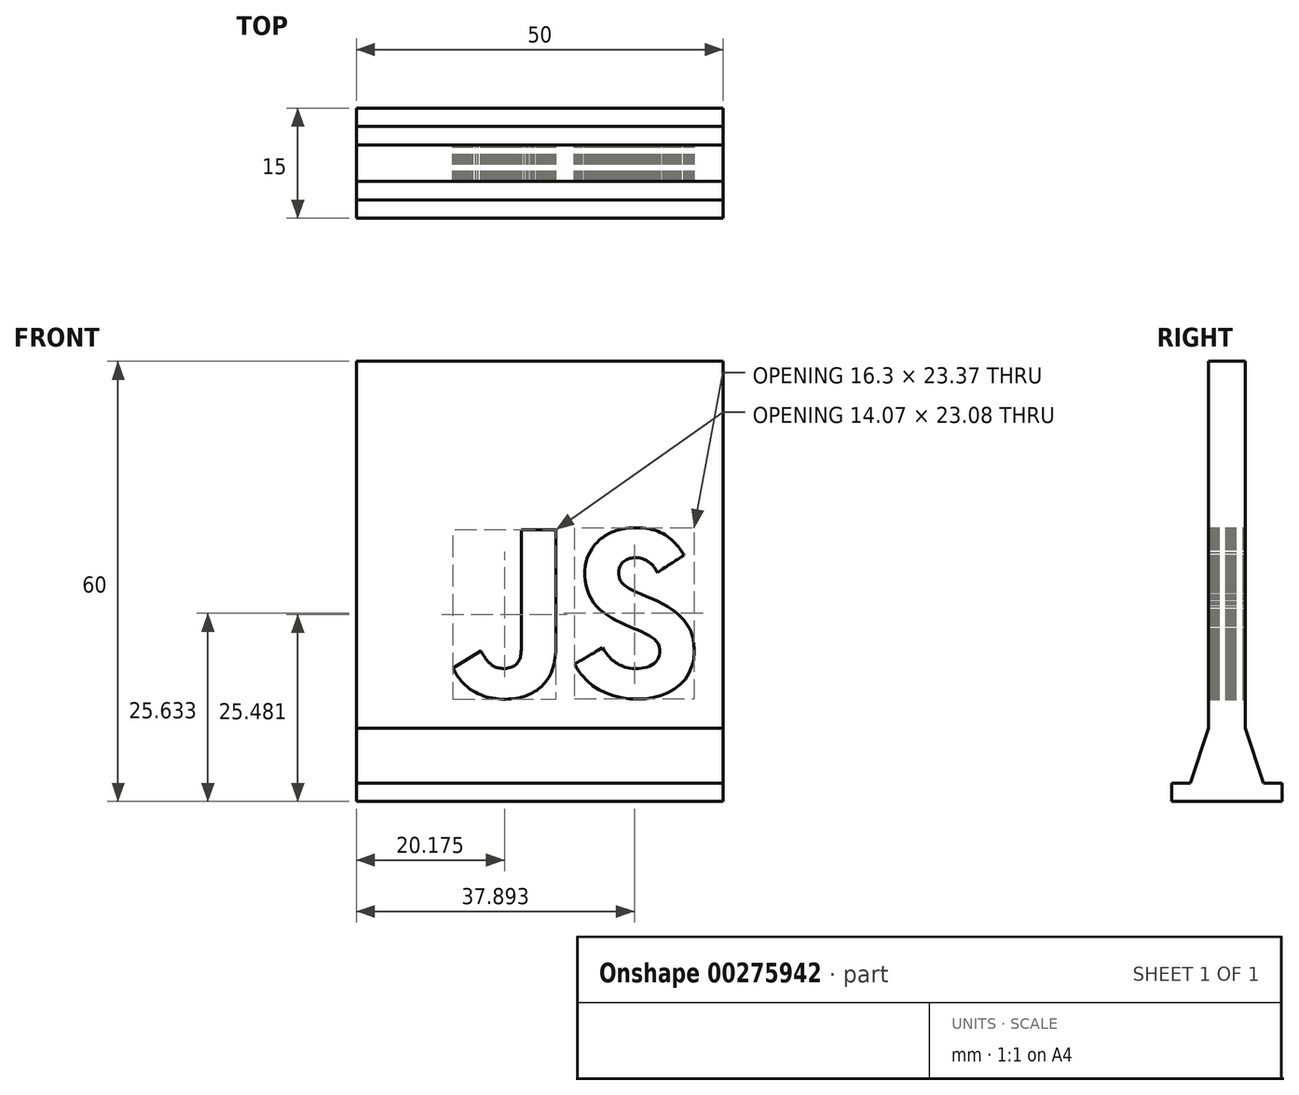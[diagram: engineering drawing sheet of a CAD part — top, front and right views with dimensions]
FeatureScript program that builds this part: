
annotation { "Feature Type Name" : "Feature", "Feature Type Description" : "" }
export const myFeature = defineFeature(function(context is Context, id is Id, definition is map)
    precondition{}
    {
        {
            var Q0;
            Q0=qCreatedBy(makeId("Front.planeOp"),FACE);
            var sketch = newSketch(context, id + "F0", { "sketchPlane" : qUnion([Q0])});
            skLineSegment(sketch, "E0", {"start": v(-25, 25) * mm, "end": v(-21.87, 25) * mm});
            skLineSegment(sketch, "E1", {"start": v(-21.87, 25) * mm, "end": v(-18.75, 25) * mm});
            skLineSegment(sketch, "E2", {"start": v(-18.75, 25) * mm, "end": v(-15.62, 25) * mm});
            skLineSegment(sketch, "E3", {"start": v(-15.62, 25) * mm, "end": v(-12.5, 25) * mm});
            skLineSegment(sketch, "E4", {"start": v(-12.5, 25) * mm, "end": v(-9.37, 25) * mm});
            skLineSegment(sketch, "E5", {"start": v(-9.37, 25) * mm, "end": v(-6.25, 25) * mm});
            skLineSegment(sketch, "E6", {"start": v(-6.25, 25) * mm, "end": v(-3.12, 25) * mm});
            skLineSegment(sketch, "E7", {"start": v(-3.12, 25) * mm, "end": v(0, 25) * mm});
            skLineSegment(sketch, "E8", {"start": v(0, 25) * mm, "end": v(3.12, 25) * mm});
            skLineSegment(sketch, "E9", {"start": v(3.12, 25) * mm, "end": v(6.25, 25) * mm});
            skLineSegment(sketch, "E10", {"start": v(6.25, 25) * mm, "end": v(9.37, 25) * mm});
            skLineSegment(sketch, "E11", {"start": v(9.37, 25) * mm, "end": v(12.5, 25) * mm});
            skLineSegment(sketch, "E12", {"start": v(12.5, 25) * mm, "end": v(15.62, 25) * mm});
            skLineSegment(sketch, "E13", {"start": v(15.62, 25) * mm, "end": v(18.75, 25) * mm});
            skLineSegment(sketch, "E14", {"start": v(18.75, 25) * mm, "end": v(21.87, 25) * mm});
            skLineSegment(sketch, "E15", {"start": v(21.87, 25) * mm, "end": v(25, 25) * mm});
            skLineSegment(sketch, "E16", {"start": v(25, 25) * mm, "end": v(25, 21.87) * mm});
            skLineSegment(sketch, "E17", {"start": v(25, 21.87) * mm, "end": v(25, 18.75) * mm});
            skLineSegment(sketch, "E18", {"start": v(25, 18.75) * mm, "end": v(25, 15.62) * mm});
            skLineSegment(sketch, "E19", {"start": v(25, 15.62) * mm, "end": v(25, 12.5) * mm});
            skLineSegment(sketch, "E20", {"start": v(25, 12.5) * mm, "end": v(25, 9.37) * mm});
            skLineSegment(sketch, "E21", {"start": v(25, 9.37) * mm, "end": v(25, 6.25) * mm});
            skLineSegment(sketch, "E22", {"start": v(25, 6.25) * mm, "end": v(25, 3.12) * mm});
            skLineSegment(sketch, "E23", {"start": v(25, 3.12) * mm, "end": v(25, 0) * mm});
            skLineSegment(sketch, "E24", {"start": v(25, 0) * mm, "end": v(25, -3.13) * mm});
            skLineSegment(sketch, "E25", {"start": v(25, -3.13) * mm, "end": v(25, -6.25) * mm});
            skLineSegment(sketch, "E26", {"start": v(25, -6.25) * mm, "end": v(25, -9.38) * mm});
            skLineSegment(sketch, "E27", {"start": v(25, -9.38) * mm, "end": v(25, -12.5) * mm});
            skLineSegment(sketch, "E28", {"start": v(25, -12.5) * mm, "end": v(25, -15.63) * mm});
            skLineSegment(sketch, "E29", {"start": v(25, -15.63) * mm, "end": v(25, -18.75) * mm});
            skLineSegment(sketch, "E30", {"start": v(25, -18.75) * mm, "end": v(25, -21.88) * mm});
            skLineSegment(sketch, "E31", {"start": v(25, -21.88) * mm, "end": v(25, -25) * mm});
            skLineSegment(sketch, "E32", {"start": v(25, -25) * mm, "end": v(21.87, -25) * mm});
            skLineSegment(sketch, "E33", {"start": v(21.87, -25) * mm, "end": v(18.75, -25) * mm});
            skLineSegment(sketch, "E34", {"start": v(18.75, -25) * mm, "end": v(15.62, -25) * mm});
            skLineSegment(sketch, "E35", {"start": v(15.62, -25) * mm, "end": v(12.5, -25) * mm});
            skLineSegment(sketch, "E36", {"start": v(12.5, -25) * mm, "end": v(9.37, -25) * mm});
            skLineSegment(sketch, "E37", {"start": v(9.37, -25) * mm, "end": v(6.25, -25) * mm});
            skLineSegment(sketch, "E38", {"start": v(6.25, -25) * mm, "end": v(3.12, -25) * mm});
            skLineSegment(sketch, "E39", {"start": v(3.12, -25) * mm, "end": v(0, -25) * mm});
            skLineSegment(sketch, "E40", {"start": v(0, -25) * mm, "end": v(-3.12, -25) * mm});
            skLineSegment(sketch, "E41", {"start": v(-3.12, -25) * mm, "end": v(-6.25, -25) * mm});
            skLineSegment(sketch, "E42", {"start": v(-6.25, -25) * mm, "end": v(-9.37, -25) * mm});
            skLineSegment(sketch, "E43", {"start": v(-9.37, -25) * mm, "end": v(-12.5, -25) * mm});
            skLineSegment(sketch, "E44", {"start": v(-12.5, -25) * mm, "end": v(-15.62, -25) * mm});
            skLineSegment(sketch, "E45", {"start": v(-15.62, -25) * mm, "end": v(-18.75, -25) * mm});
            skLineSegment(sketch, "E46", {"start": v(-18.75, -25) * mm, "end": v(-21.87, -25) * mm});
            skLineSegment(sketch, "E47", {"start": v(-21.87, -25) * mm, "end": v(-25, -25) * mm});
            skLineSegment(sketch, "E48", {"start": v(-25, -25) * mm, "end": v(-25, -21.88) * mm});
            skLineSegment(sketch, "E49", {"start": v(-25, -21.88) * mm, "end": v(-25, -18.75) * mm});
            skLineSegment(sketch, "E50", {"start": v(-25, -18.75) * mm, "end": v(-25, -15.63) * mm});
            skLineSegment(sketch, "E51", {"start": v(-25, -15.63) * mm, "end": v(-25, -12.5) * mm});
            skLineSegment(sketch, "E52", {"start": v(-25, -12.5) * mm, "end": v(-25, -9.38) * mm});
            skLineSegment(sketch, "E53", {"start": v(-25, -9.38) * mm, "end": v(-25, -6.25) * mm});
            skLineSegment(sketch, "E54", {"start": v(-25, -6.25) * mm, "end": v(-25, -3.13) * mm});
            skLineSegment(sketch, "E55", {"start": v(-25, -3.13) * mm, "end": v(-25, 0) * mm});
            skLineSegment(sketch, "E56", {"start": v(-25, 0) * mm, "end": v(-25, 3.12) * mm});
            skLineSegment(sketch, "E57", {"start": v(-25, 3.12) * mm, "end": v(-25, 6.25) * mm});
            skLineSegment(sketch, "E58", {"start": v(-25, 6.25) * mm, "end": v(-25, 9.37) * mm});
            skLineSegment(sketch, "E59", {"start": v(-25, 9.37) * mm, "end": v(-25, 12.5) * mm});
            skLineSegment(sketch, "E60", {"start": v(-25, 12.5) * mm, "end": v(-25, 15.62) * mm});
            skLineSegment(sketch, "E61", {"start": v(-25, 15.62) * mm, "end": v(-25, 18.75) * mm});
            skLineSegment(sketch, "E62", {"start": v(-25, 18.75) * mm, "end": v(-25, 21.87) * mm});
            skLineSegment(sketch, "E63", {"start": v(-25, 21.87) * mm, "end": v(-25, 25) * mm});
            skLineSegment(sketch, "E64", {"start": v(20.9, -13.07) * mm, "end": v(20.83, -12.65) * mm});
            skLineSegment(sketch, "E65", {"start": v(20.83, -12.65) * mm, "end": v(20.71, -12.24) * mm});
            skLineSegment(sketch, "E66", {"start": v(20.71, -12.24) * mm, "end": v(20.57, -11.83) * mm});
            skLineSegment(sketch, "E67", {"start": v(20.57, -11.83) * mm, "end": v(20.4, -11.43) * mm});
            skLineSegment(sketch, "E68", {"start": v(20.4, -11.43) * mm, "end": v(20.18, -11.04) * mm});
            skLineSegment(sketch, "E69", {"start": v(20.18, -11.04) * mm, "end": v(19.93, -10.65) * mm});
            skLineSegment(sketch, "E70", {"start": v(19.93, -10.65) * mm, "end": v(19.63, -10.27) * mm});
            skLineSegment(sketch, "E71", {"start": v(19.63, -10.27) * mm, "end": v(19.3, -9.9) * mm});
            skLineSegment(sketch, "E72", {"start": v(19.3, -9.9) * mm, "end": v(18.9, -9.53) * mm});
            skLineSegment(sketch, "E73", {"start": v(18.9, -9.53) * mm, "end": v(18.47, -9.17) * mm});
            skLineSegment(sketch, "E74", {"start": v(18.47, -9.17) * mm, "end": v(17.98, -8.81) * mm});
            skLineSegment(sketch, "E75", {"start": v(17.98, -8.81) * mm, "end": v(17.43, -8.46) * mm});
            skLineSegment(sketch, "E76", {"start": v(17.43, -8.46) * mm, "end": v(16.83, -8.11) * mm});
            skLineSegment(sketch, "E77", {"start": v(16.83, -8.11) * mm, "end": v(16.17, -7.77) * mm});
            skLineSegment(sketch, "E78", {"start": v(16.17, -7.77) * mm, "end": v(15.44, -7.43) * mm});
            skLineSegment(sketch, "E79", {"start": v(15.44, -7.43) * mm, "end": v(14.65, -7.1) * mm});
            skLineSegment(sketch, "E80", {"start": v(14.65, -7.1) * mm, "end": v(14.36, -6.96) * mm});
            skLineSegment(sketch, "E81", {"start": v(14.36, -6.96) * mm, "end": v(14.07, -6.84) * mm});
            skLineSegment(sketch, "E82", {"start": v(14.07, -6.84) * mm, "end": v(13.78, -6.71) * mm});
            skLineSegment(sketch, "E83", {"start": v(13.78, -6.71) * mm, "end": v(13.49, -6.59) * mm});
            skLineSegment(sketch, "E84", {"start": v(13.49, -6.59) * mm, "end": v(13.2, -6.46) * mm});
            skLineSegment(sketch, "E85", {"start": v(13.2, -6.46) * mm, "end": v(12.92, -6.34) * mm});
            skLineSegment(sketch, "E86", {"start": v(12.92, -6.34) * mm, "end": v(12.65, -6.21) * mm});
            skLineSegment(sketch, "E87", {"start": v(12.65, -6.21) * mm, "end": v(12.4, -6.08) * mm});
            skLineSegment(sketch, "E88", {"start": v(12.4, -6.08) * mm, "end": v(12.14, -5.94) * mm});
            skLineSegment(sketch, "E89", {"start": v(12.14, -5.94) * mm, "end": v(11.9, -5.8) * mm});
            skLineSegment(sketch, "E90", {"start": v(11.9, -5.8) * mm, "end": v(11.69, -5.65) * mm});
            skLineSegment(sketch, "E91", {"start": v(11.69, -5.65) * mm, "end": v(11.49, -5.48) * mm});
            skLineSegment(sketch, "E92", {"start": v(11.49, -5.48) * mm, "end": v(11.3, -5.31) * mm});
            skLineSegment(sketch, "E93", {"start": v(11.3, -5.31) * mm, "end": v(11.15, -5.13) * mm});
            skLineSegment(sketch, "E94", {"start": v(11.15, -5.13) * mm, "end": v(11.01, -4.93) * mm});
            skLineSegment(sketch, "E95", {"start": v(11.01, -4.93) * mm, "end": v(10.9, -4.72) * mm});
            skLineSegment(sketch, "E96", {"start": v(10.9, -4.72) * mm, "end": v(10.87, -4.6) * mm});
            skLineSegment(sketch, "E97", {"start": v(10.87, -4.6) * mm, "end": v(10.84, -4.48) * mm});
            skLineSegment(sketch, "E98", {"start": v(10.84, -4.48) * mm, "end": v(10.82, -4.37) * mm});
            skLineSegment(sketch, "E99", {"start": v(10.82, -4.37) * mm, "end": v(10.8, -4.27) * mm});
            skLineSegment(sketch, "E100", {"start": v(10.8, -4.27) * mm, "end": v(10.78, -4.17) * mm});
            skLineSegment(sketch, "E101", {"start": v(10.78, -4.17) * mm, "end": v(10.77, -4.07) * mm});
            skLineSegment(sketch, "E102", {"start": v(10.77, -4.07) * mm, "end": v(10.75, -3.98) * mm});
            skLineSegment(sketch, "E103", {"start": v(10.75, -3.98) * mm, "end": v(10.75, -3.9) * mm});
            skLineSegment(sketch, "E104", {"start": v(10.75, -3.9) * mm, "end": v(10.74, -3.8) * mm});
            skLineSegment(sketch, "E105", {"start": v(10.74, -3.8) * mm, "end": v(10.74, -3.73) * mm});
            skLineSegment(sketch, "E106", {"start": v(10.74, -3.73) * mm, "end": v(10.75, -3.65) * mm});
            skLineSegment(sketch, "E107", {"start": v(10.75, -3.65) * mm, "end": v(10.75, -3.57) * mm});
            skLineSegment(sketch, "E108", {"start": v(10.75, -3.57) * mm, "end": v(10.76, -3.49) * mm});
            skLineSegment(sketch, "E109", {"start": v(10.76, -3.49) * mm, "end": v(10.78, -3.41) * mm});
            skLineSegment(sketch, "E110", {"start": v(10.78, -3.41) * mm, "end": v(10.8, -3.34) * mm});
            skLineSegment(sketch, "E111", {"start": v(10.8, -3.34) * mm, "end": v(10.81, -3.26) * mm});
            skLineSegment(sketch, "E112", {"start": v(10.81, -3.26) * mm, "end": v(10.89, -3.02) * mm});
            skLineSegment(sketch, "E113", {"start": v(10.89, -3.02) * mm, "end": v(11, -2.8) * mm});
            skLineSegment(sketch, "E114", {"start": v(11, -2.8) * mm, "end": v(11.12, -2.61) * mm});
            skLineSegment(sketch, "E115", {"start": v(11.12, -2.61) * mm, "end": v(11.27, -2.44) * mm});
            skLineSegment(sketch, "E116", {"start": v(11.27, -2.44) * mm, "end": v(11.44, -2.28) * mm});
            skLineSegment(sketch, "E117", {"start": v(11.44, -2.28) * mm, "end": v(11.63, -2.15) * mm});
            skLineSegment(sketch, "E118", {"start": v(11.63, -2.15) * mm, "end": v(11.83, -2.03) * mm});
            skLineSegment(sketch, "E119", {"start": v(11.83, -2.03) * mm, "end": v(12.05, -1.94) * mm});
            skLineSegment(sketch, "E120", {"start": v(12.05, -1.94) * mm, "end": v(12.28, -1.87) * mm});
            skLineSegment(sketch, "E121", {"start": v(12.28, -1.87) * mm, "end": v(12.51, -1.81) * mm});
            skLineSegment(sketch, "E122", {"start": v(12.51, -1.81) * mm, "end": v(12.75, -1.78) * mm});
            skLineSegment(sketch, "E123", {"start": v(12.75, -1.78) * mm, "end": v(13, -1.77) * mm});
            skLineSegment(sketch, "E124", {"start": v(13, -1.77) * mm, "end": v(13.25, -1.77) * mm});
            skLineSegment(sketch, "E125", {"start": v(13.25, -1.77) * mm, "end": v(13.5, -1.8) * mm});
            skLineSegment(sketch, "E126", {"start": v(13.5, -1.8) * mm, "end": v(13.74, -1.84) * mm});
            skLineSegment(sketch, "E127", {"start": v(13.74, -1.84) * mm, "end": v(13.98, -1.9) * mm});
            skLineSegment(sketch, "E128", {"start": v(13.98, -1.9) * mm, "end": v(14.13, -1.96) * mm});
            skLineSegment(sketch, "E129", {"start": v(14.13, -1.96) * mm, "end": v(14.28, -2.02) * mm});
            skLineSegment(sketch, "E130", {"start": v(14.28, -2.02) * mm, "end": v(14.43, -2.1) * mm});
            skLineSegment(sketch, "E131", {"start": v(14.43, -2.1) * mm, "end": v(14.57, -2.17) * mm});
            skLineSegment(sketch, "E132", {"start": v(14.57, -2.17) * mm, "end": v(14.72, -2.26) * mm});
            skLineSegment(sketch, "E133", {"start": v(14.72, -2.26) * mm, "end": v(14.86, -2.36) * mm});
            skLineSegment(sketch, "E134", {"start": v(14.86, -2.36) * mm, "end": v(15, -2.46) * mm});
            skLineSegment(sketch, "E135", {"start": v(15, -2.46) * mm, "end": v(15.13, -2.57) * mm});
            skLineSegment(sketch, "E136", {"start": v(15.13, -2.57) * mm, "end": v(15.25, -2.7) * mm});
            skLineSegment(sketch, "E137", {"start": v(15.25, -2.7) * mm, "end": v(15.38, -2.83) * mm});
            skLineSegment(sketch, "E138", {"start": v(15.38, -2.83) * mm, "end": v(15.5, -2.96) * mm});
            skLineSegment(sketch, "E139", {"start": v(15.5, -2.96) * mm, "end": v(15.61, -3.11) * mm});
            skLineSegment(sketch, "E140", {"start": v(15.61, -3.11) * mm, "end": v(15.72, -3.27) * mm});
            skLineSegment(sketch, "E141", {"start": v(15.72, -3.27) * mm, "end": v(15.83, -3.43) * mm});
            skLineSegment(sketch, "E142", {"start": v(15.83, -3.43) * mm, "end": v(15.92, -3.6) * mm});
            skLineSegment(sketch, "E143", {"start": v(15.92, -3.6) * mm, "end": v(16.01, -3.79) * mm});
            skLineSegment(sketch, "E144", {"start": v(16.01, -3.79) * mm, "end": v(16.4, -3.54) * mm});
            skLineSegment(sketch, "E145", {"start": v(16.4, -3.54) * mm, "end": v(16.73, -3.33) * mm});
            skLineSegment(sketch, "E146", {"start": v(16.73, -3.33) * mm, "end": v(17.02, -3.13) * mm});
            skLineSegment(sketch, "E147", {"start": v(17.02, -3.13) * mm, "end": v(17.28, -2.97) * mm});
            skLineSegment(sketch, "E148", {"start": v(17.28, -2.97) * mm, "end": v(17.51, -2.82) * mm});
            skLineSegment(sketch, "E149", {"start": v(17.51, -2.82) * mm, "end": v(17.72, -2.68) * mm});
            skLineSegment(sketch, "E150", {"start": v(17.72, -2.68) * mm, "end": v(17.91, -2.56) * mm});
            skLineSegment(sketch, "E151", {"start": v(17.91, -2.56) * mm, "end": v(18.09, -2.45) * mm});
            skLineSegment(sketch, "E152", {"start": v(18.09, -2.45) * mm, "end": v(18.25, -2.34) * mm});
            skLineSegment(sketch, "E153", {"start": v(18.25, -2.34) * mm, "end": v(18.42, -2.24) * mm});
            skLineSegment(sketch, "E154", {"start": v(18.42, -2.24) * mm, "end": v(18.6, -2.13) * mm});
            skLineSegment(sketch, "E155", {"start": v(18.6, -2.13) * mm, "end": v(18.77, -2.02) * mm});
            skLineSegment(sketch, "E156", {"start": v(18.77, -2.02) * mm, "end": v(18.96, -1.9) * mm});
            skLineSegment(sketch, "E157", {"start": v(18.96, -1.9) * mm, "end": v(19.17, -1.76) * mm});
            skLineSegment(sketch, "E158", {"start": v(19.17, -1.76) * mm, "end": v(19.4, -1.6) * mm});
            skLineSegment(sketch, "E159", {"start": v(19.4, -1.6) * mm, "end": v(19.67, -1.44) * mm});
            skLineSegment(sketch, "E160", {"start": v(19.67, -1.44) * mm, "end": v(19.57, -1.29) * mm});
            skLineSegment(sketch, "E161", {"start": v(19.57, -1.29) * mm, "end": v(19.48, -1.14) * mm});
            skLineSegment(sketch, "E162", {"start": v(19.48, -1.14) * mm, "end": v(19.39, -1) * mm});
            skLineSegment(sketch, "E163", {"start": v(19.39, -1) * mm, "end": v(19.3, -0.88) * mm});
            skLineSegment(sketch, "E164", {"start": v(19.3, -0.88) * mm, "end": v(19.22, -0.76) * mm});
            skLineSegment(sketch, "E165", {"start": v(19.22, -0.76) * mm, "end": v(19.14, -0.65) * mm});
            skLineSegment(sketch, "E166", {"start": v(19.14, -0.65) * mm, "end": v(19.07, -0.55) * mm});
            skLineSegment(sketch, "E167", {"start": v(19.07, -0.55) * mm, "end": v(19, -0.45) * mm});
            skLineSegment(sketch, "E168", {"start": v(19, -0.45) * mm, "end": v(18.93, -0.36) * mm});
            skLineSegment(sketch, "E169", {"start": v(18.93, -0.36) * mm, "end": v(18.86, -0.27) * mm});
            skLineSegment(sketch, "E170", {"start": v(18.86, -0.27) * mm, "end": v(18.8, -0.19) * mm});
            skLineSegment(sketch, "E171", {"start": v(18.8, -0.19) * mm, "end": v(18.73, -0.11) * mm});
            skLineSegment(sketch, "E172", {"start": v(18.73, -0.11) * mm, "end": v(18.66, -0.04) * mm});
            skLineSegment(sketch, "E173", {"start": v(18.66, -0.04) * mm, "end": v(18.6, 0.04) * mm});
            skLineSegment(sketch, "E174", {"start": v(18.6, 0.04) * mm, "end": v(18.53, 0.1) * mm});
            skLineSegment(sketch, "E175", {"start": v(18.53, 0.1) * mm, "end": v(18.47, 0.18) * mm});
            skLineSegment(sketch, "E176", {"start": v(18.47, 0.18) * mm, "end": v(18.22, 0.44) * mm});
            skLineSegment(sketch, "E177", {"start": v(18.22, 0.44) * mm, "end": v(17.96, 0.69) * mm});
            skLineSegment(sketch, "E178", {"start": v(17.96, 0.69) * mm, "end": v(17.68, 0.92) * mm});
            skLineSegment(sketch, "E179", {"start": v(17.68, 0.92) * mm, "end": v(17.4, 1.13) * mm});
            skLineSegment(sketch, "E180", {"start": v(17.4, 1.13) * mm, "end": v(17.1, 1.33) * mm});
            skLineSegment(sketch, "E181", {"start": v(17.1, 1.33) * mm, "end": v(16.78, 1.5) * mm});
            skLineSegment(sketch, "E182", {"start": v(16.78, 1.5) * mm, "end": v(16.44, 1.67) * mm});
            skLineSegment(sketch, "E183", {"start": v(16.44, 1.67) * mm, "end": v(16.1, 1.8) * mm});
            skLineSegment(sketch, "E184", {"start": v(16.1, 1.8) * mm, "end": v(15.72, 1.94) * mm});
            skLineSegment(sketch, "E185", {"start": v(15.72, 1.94) * mm, "end": v(15.34, 2.04) * mm});
            skLineSegment(sketch, "E186", {"start": v(15.34, 2.04) * mm, "end": v(14.93, 2.14) * mm});
            skLineSegment(sketch, "E187", {"start": v(14.93, 2.14) * mm, "end": v(14.5, 2.2) * mm});
            skLineSegment(sketch, "E188", {"start": v(14.5, 2.2) * mm, "end": v(14.05, 2.26) * mm});
            skLineSegment(sketch, "E189", {"start": v(14.05, 2.26) * mm, "end": v(13.58, 2.3) * mm});
            skLineSegment(sketch, "E190", {"start": v(13.58, 2.3) * mm, "end": v(13.09, 2.32) * mm});
            skLineSegment(sketch, "E191", {"start": v(13.09, 2.32) * mm, "end": v(12.57, 2.31) * mm});
            skLineSegment(sketch, "E192", {"start": v(12.57, 2.31) * mm, "end": v(12.48, 2.3) * mm});
            skLineSegment(sketch, "E193", {"start": v(12.48, 2.3) * mm, "end": v(12.39, 2.3) * mm});
            skLineSegment(sketch, "E194", {"start": v(12.39, 2.3) * mm, "end": v(12.3, 2.28) * mm});
            skLineSegment(sketch, "E195", {"start": v(12.3, 2.28) * mm, "end": v(12.2, 2.27) * mm});
            skLineSegment(sketch, "E196", {"start": v(12.2, 2.27) * mm, "end": v(12.11, 2.25) * mm});
            skLineSegment(sketch, "E197", {"start": v(12.11, 2.25) * mm, "end": v(12.02, 2.24) * mm});
            skLineSegment(sketch, "E198", {"start": v(12.02, 2.24) * mm, "end": v(11.93, 2.23) * mm});
            skLineSegment(sketch, "E199", {"start": v(11.93, 2.23) * mm, "end": v(11.83, 2.22) * mm});
            skLineSegment(sketch, "E200", {"start": v(11.83, 2.22) * mm, "end": v(11.74, 2.2) * mm});
            skLineSegment(sketch, "E201", {"start": v(11.74, 2.2) * mm, "end": v(11.65, 2.2) * mm});
            skLineSegment(sketch, "E202", {"start": v(11.65, 2.2) * mm, "end": v(11.56, 2.18) * mm});
            skLineSegment(sketch, "E203", {"start": v(11.56, 2.18) * mm, "end": v(11.47, 2.17) * mm});
            skLineSegment(sketch, "E204", {"start": v(11.47, 2.17) * mm, "end": v(11.37, 2.16) * mm});
            skLineSegment(sketch, "E205", {"start": v(11.37, 2.16) * mm, "end": v(11.28, 2.15) * mm});
            skLineSegment(sketch, "E206", {"start": v(11.28, 2.15) * mm, "end": v(11.2, 2.14) * mm});
            skLineSegment(sketch, "E207", {"start": v(11.2, 2.14) * mm, "end": v(11.1, 2.12) * mm});
            skLineSegment(sketch, "E208", {"start": v(11.1, 2.12) * mm, "end": v(10.83, 2.05) * mm});
            skLineSegment(sketch, "E209", {"start": v(10.83, 2.05) * mm, "end": v(10.57, 1.97) * mm});
            skLineSegment(sketch, "E210", {"start": v(10.57, 1.97) * mm, "end": v(10.31, 1.88) * mm});
            skLineSegment(sketch, "E211", {"start": v(10.31, 1.88) * mm, "end": v(10.06, 1.79) * mm});
            skLineSegment(sketch, "E212", {"start": v(10.06, 1.79) * mm, "end": v(9.8, 1.68) * mm});
            skLineSegment(sketch, "E213", {"start": v(9.8, 1.68) * mm, "end": v(9.56, 1.57) * mm});
            skLineSegment(sketch, "E214", {"start": v(9.56, 1.57) * mm, "end": v(9.32, 1.45) * mm});
            skLineSegment(sketch, "E215", {"start": v(9.32, 1.45) * mm, "end": v(9.1, 1.32) * mm});
            skLineSegment(sketch, "E216", {"start": v(9.1, 1.32) * mm, "end": v(8.87, 1.18) * mm});
            skLineSegment(sketch, "E217", {"start": v(8.87, 1.18) * mm, "end": v(8.65, 1.04) * mm});
            skLineSegment(sketch, "E218", {"start": v(8.65, 1.04) * mm, "end": v(8.44, 0.89) * mm});
            skLineSegment(sketch, "E219", {"start": v(8.44, 0.89) * mm, "end": v(8.24, 0.73) * mm});
            skLineSegment(sketch, "E220", {"start": v(8.24, 0.73) * mm, "end": v(8.05, 0.56) * mm});
            skLineSegment(sketch, "E221", {"start": v(8.05, 0.56) * mm, "end": v(7.87, 0.4) * mm});
            skLineSegment(sketch, "E222", {"start": v(7.87, 0.4) * mm, "end": v(7.7, 0.22) * mm});
            skLineSegment(sketch, "E223", {"start": v(7.7, 0.22) * mm, "end": v(7.55, 0.03) * mm});
            skLineSegment(sketch, "E224", {"start": v(7.55, 0.03) * mm, "end": v(7.14, -0.5) * mm});
            skLineSegment(sketch, "E225", {"start": v(7.14, -0.5) * mm, "end": v(6.8, -1.06) * mm});
            skLineSegment(sketch, "E226", {"start": v(6.8, -1.06) * mm, "end": v(6.54, -1.66) * mm});
            skLineSegment(sketch, "E227", {"start": v(6.54, -1.66) * mm, "end": v(6.33, -2.28) * mm});
            skLineSegment(sketch, "E228", {"start": v(6.33, -2.28) * mm, "end": v(6.2, -2.93) * mm});
            skLineSegment(sketch, "E229", {"start": v(6.2, -2.93) * mm, "end": v(6.13, -3.59) * mm});
            skLineSegment(sketch, "E230", {"start": v(6.13, -3.59) * mm, "end": v(6.12, -4.25) * mm});
            skLineSegment(sketch, "E231", {"start": v(6.12, -4.25) * mm, "end": v(6.18, -4.9) * mm});
            skLineSegment(sketch, "E232", {"start": v(6.18, -4.9) * mm, "end": v(6.3, -5.56) * mm});
            skLineSegment(sketch, "E233", {"start": v(6.3, -5.56) * mm, "end": v(6.48, -6.2) * mm});
            skLineSegment(sketch, "E234", {"start": v(6.48, -6.2) * mm, "end": v(6.71, -6.8) * mm});
            skLineSegment(sketch, "E235", {"start": v(6.71, -6.8) * mm, "end": v(7, -7.4) * mm});
            skLineSegment(sketch, "E236", {"start": v(7, -7.4) * mm, "end": v(7.36, -7.94) * mm});
            skLineSegment(sketch, "E237", {"start": v(7.36, -7.94) * mm, "end": v(7.77, -8.44) * mm});
            skLineSegment(sketch, "E238", {"start": v(7.77, -8.44) * mm, "end": v(8.23, -8.9) * mm});
            skLineSegment(sketch, "E239", {"start": v(8.23, -8.9) * mm, "end": v(8.74, -9.29) * mm});
            skLineSegment(sketch, "E240", {"start": v(8.74, -9.29) * mm, "end": v(9.29, -9.67) * mm});
            skLineSegment(sketch, "E241", {"start": v(9.29, -9.67) * mm, "end": v(9.86, -10.01) * mm});
            skLineSegment(sketch, "E242", {"start": v(9.86, -10.01) * mm, "end": v(10.44, -10.33) * mm});
            skLineSegment(sketch, "E243", {"start": v(10.44, -10.33) * mm, "end": v(11.04, -10.63) * mm});
            skLineSegment(sketch, "E244", {"start": v(11.04, -10.63) * mm, "end": v(11.64, -10.9) * mm});
            skLineSegment(sketch, "E245", {"start": v(11.64, -10.9) * mm, "end": v(12.23, -11.16) * mm});
            skLineSegment(sketch, "E246", {"start": v(12.23, -11.16) * mm, "end": v(12.81, -11.4) * mm});
            skLineSegment(sketch, "E247", {"start": v(12.81, -11.4) * mm, "end": v(13.37, -11.64) * mm});
            skLineSegment(sketch, "E248", {"start": v(13.37, -11.64) * mm, "end": v(13.9, -11.88) * mm});
            skLineSegment(sketch, "E249", {"start": v(13.9, -11.88) * mm, "end": v(14.4, -12.12) * mm});
            skLineSegment(sketch, "E250", {"start": v(14.4, -12.12) * mm, "end": v(14.87, -12.37) * mm});
            skLineSegment(sketch, "E251", {"start": v(14.87, -12.37) * mm, "end": v(15.28, -12.63) * mm});
            skLineSegment(sketch, "E252", {"start": v(15.28, -12.63) * mm, "end": v(15.63, -12.91) * mm});
            skLineSegment(sketch, "E253", {"start": v(15.63, -12.91) * mm, "end": v(15.92, -13.21) * mm});
            skLineSegment(sketch, "E254", {"start": v(15.92, -13.21) * mm, "end": v(16.14, -13.54) * mm});
            skLineSegment(sketch, "E255", {"start": v(16.14, -13.54) * mm, "end": v(16.28, -13.9) * mm});
            skLineSegment(sketch, "E256", {"start": v(16.28, -13.9) * mm, "end": v(16.34, -14.33) * mm});
            skLineSegment(sketch, "E257", {"start": v(16.34, -14.33) * mm, "end": v(16.35, -14.73) * mm});
            skLineSegment(sketch, "E258", {"start": v(16.35, -14.73) * mm, "end": v(16.3, -15.1) * mm});
            skLineSegment(sketch, "E259", {"start": v(16.3, -15.1) * mm, "end": v(16.18, -15.42) * mm});
            skLineSegment(sketch, "E260", {"start": v(16.18, -15.42) * mm, "end": v(16.02, -15.71) * mm});
            skLineSegment(sketch, "E261", {"start": v(16.02, -15.71) * mm, "end": v(15.82, -15.97) * mm});
            skLineSegment(sketch, "E262", {"start": v(15.82, -15.97) * mm, "end": v(15.57, -16.2) * mm});
            skLineSegment(sketch, "E263", {"start": v(15.57, -16.2) * mm, "end": v(15.3, -16.39) * mm});
            skLineSegment(sketch, "E264", {"start": v(15.3, -16.39) * mm, "end": v(14.97, -16.54) * mm});
            skLineSegment(sketch, "E265", {"start": v(14.97, -16.54) * mm, "end": v(14.63, -16.67) * mm});
            skLineSegment(sketch, "E266", {"start": v(14.63, -16.67) * mm, "end": v(14.26, -16.77) * mm});
            skLineSegment(sketch, "E267", {"start": v(14.26, -16.77) * mm, "end": v(13.87, -16.84) * mm});
            skLineSegment(sketch, "E268", {"start": v(13.87, -16.84) * mm, "end": v(13.47, -16.88) * mm});
            skLineSegment(sketch, "E269", {"start": v(13.47, -16.88) * mm, "end": v(13.05, -16.9) * mm});
            skLineSegment(sketch, "E270", {"start": v(13.05, -16.9) * mm, "end": v(12.62, -16.88) * mm});
            skLineSegment(sketch, "E271", {"start": v(12.62, -16.88) * mm, "end": v(12.2, -16.84) * mm});
            skLineSegment(sketch, "E272", {"start": v(12.2, -16.84) * mm, "end": v(11.88, -16.77) * mm});
            skLineSegment(sketch, "E273", {"start": v(11.88, -16.77) * mm, "end": v(11.6, -16.68) * mm});
            skLineSegment(sketch, "E274", {"start": v(11.6, -16.68) * mm, "end": v(11.31, -16.59) * mm});
            skLineSegment(sketch, "E275", {"start": v(11.31, -16.59) * mm, "end": v(11.05, -16.48) * mm});
            skLineSegment(sketch, "E276", {"start": v(11.05, -16.48) * mm, "end": v(10.8, -16.35) * mm});
            skLineSegment(sketch, "E277", {"start": v(10.8, -16.35) * mm, "end": v(10.56, -16.22) * mm});
            skLineSegment(sketch, "E278", {"start": v(10.56, -16.22) * mm, "end": v(10.33, -16.07) * mm});
            skLineSegment(sketch, "E279", {"start": v(10.33, -16.07) * mm, "end": v(10.11, -15.9) * mm});
            skLineSegment(sketch, "E280", {"start": v(10.11, -15.9) * mm, "end": v(9.9, -15.73) * mm});
            skLineSegment(sketch, "E281", {"start": v(9.9, -15.73) * mm, "end": v(9.7, -15.54) * mm});
            skLineSegment(sketch, "E282", {"start": v(9.7, -15.54) * mm, "end": v(9.5, -15.33) * mm});
            skLineSegment(sketch, "E283", {"start": v(9.5, -15.33) * mm, "end": v(9.3, -15.1) * mm});
            skLineSegment(sketch, "E284", {"start": v(9.3, -15.1) * mm, "end": v(9.11, -14.87) * mm});
            skLineSegment(sketch, "E285", {"start": v(9.11, -14.87) * mm, "end": v(8.92, -14.62) * mm});
            skLineSegment(sketch, "E286", {"start": v(8.92, -14.62) * mm, "end": v(8.73, -14.35) * mm});
            skLineSegment(sketch, "E287", {"start": v(8.73, -14.35) * mm, "end": v(8.54, -14.06) * mm});
            skLineSegment(sketch, "E288", {"start": v(8.54, -14.06) * mm, "end": v(8.21, -14.26) * mm});
            skLineSegment(sketch, "E289", {"start": v(8.21, -14.26) * mm, "end": v(7.92, -14.42) * mm});
            skLineSegment(sketch, "E290", {"start": v(7.92, -14.42) * mm, "end": v(7.66, -14.57) * mm});
            skLineSegment(sketch, "E291", {"start": v(7.66, -14.57) * mm, "end": v(7.43, -14.7) * mm});
            skLineSegment(sketch, "E292", {"start": v(7.43, -14.7) * mm, "end": v(7.22, -14.83) * mm});
            skLineSegment(sketch, "E293", {"start": v(7.22, -14.83) * mm, "end": v(7.02, -14.94) * mm});
            skLineSegment(sketch, "E294", {"start": v(7.02, -14.94) * mm, "end": v(6.84, -15.05) * mm});
            skLineSegment(sketch, "E295", {"start": v(6.84, -15.05) * mm, "end": v(6.66, -15.15) * mm});
            skLineSegment(sketch, "E296", {"start": v(6.66, -15.15) * mm, "end": v(6.48, -15.25) * mm});
            skLineSegment(sketch, "E297", {"start": v(6.48, -15.25) * mm, "end": v(6.3, -15.36) * mm});
            skLineSegment(sketch, "E298", {"start": v(6.3, -15.36) * mm, "end": v(6.1, -15.47) * mm});
            skLineSegment(sketch, "E299", {"start": v(6.1, -15.47) * mm, "end": v(5.89, -15.6) * mm});
            skLineSegment(sketch, "E300", {"start": v(5.89, -15.6) * mm, "end": v(5.65, -15.73) * mm});
            skLineSegment(sketch, "E301", {"start": v(5.65, -15.73) * mm, "end": v(5.38, -15.89) * mm});
            skLineSegment(sketch, "E302", {"start": v(5.38, -15.89) * mm, "end": v(5.08, -16.06) * mm});
            skLineSegment(sketch, "E303", {"start": v(5.08, -16.06) * mm, "end": v(4.74, -16.25) * mm});
            skLineSegment(sketch, "E304", {"start": v(4.74, -16.25) * mm, "end": v(4.83, -16.44) * mm});
            skLineSegment(sketch, "E305", {"start": v(4.83, -16.44) * mm, "end": v(4.92, -16.6) * mm});
            skLineSegment(sketch, "E306", {"start": v(4.92, -16.6) * mm, "end": v(5, -16.77) * mm});
            skLineSegment(sketch, "E307", {"start": v(5, -16.77) * mm, "end": v(5.1, -16.92) * mm});
            skLineSegment(sketch, "E308", {"start": v(5.1, -16.92) * mm, "end": v(5.19, -17.06) * mm});
            skLineSegment(sketch, "E309", {"start": v(5.19, -17.06) * mm, "end": v(5.28, -17.2) * mm});
            skLineSegment(sketch, "E310", {"start": v(5.28, -17.2) * mm, "end": v(5.38, -17.33) * mm});
            skLineSegment(sketch, "E311", {"start": v(5.38, -17.33) * mm, "end": v(5.48, -17.46) * mm});
            skLineSegment(sketch, "E312", {"start": v(5.48, -17.46) * mm, "end": v(5.58, -17.6) * mm});
            skLineSegment(sketch, "E313", {"start": v(5.58, -17.6) * mm, "end": v(5.7, -17.72) * mm});
            skLineSegment(sketch, "E314", {"start": v(5.7, -17.72) * mm, "end": v(5.8, -17.85) * mm});
            skLineSegment(sketch, "E315", {"start": v(5.8, -17.85) * mm, "end": v(5.92, -17.98) * mm});
            skLineSegment(sketch, "E316", {"start": v(5.92, -17.98) * mm, "end": v(6.04, -18.12) * mm});
            skLineSegment(sketch, "E317", {"start": v(6.04, -18.12) * mm, "end": v(6.17, -18.26) * mm});
            skLineSegment(sketch, "E318", {"start": v(6.17, -18.26) * mm, "end": v(6.3, -18.41) * mm});
            skLineSegment(sketch, "E319", {"start": v(6.3, -18.41) * mm, "end": v(6.45, -18.57) * mm});
            skLineSegment(sketch, "E320", {"start": v(6.45, -18.57) * mm, "end": v(7.18, -19.21) * mm});
            skLineSegment(sketch, "E321", {"start": v(7.18, -19.21) * mm, "end": v(8.03, -19.76) * mm});
            skLineSegment(sketch, "E322", {"start": v(8.03, -19.76) * mm, "end": v(8.97, -20.22) * mm});
            skLineSegment(sketch, "E323", {"start": v(8.97, -20.22) * mm, "end": v(9.98, -20.58) * mm});
            skLineSegment(sketch, "E324", {"start": v(9.98, -20.58) * mm, "end": v(11.04, -20.84) * mm});
            skLineSegment(sketch, "E325", {"start": v(11.04, -20.84) * mm, "end": v(12.14, -21) * mm});
            skLineSegment(sketch, "E326", {"start": v(12.14, -21) * mm, "end": v(13.25, -21.05) * mm});
            skLineSegment(sketch, "E327", {"start": v(13.25, -21.05) * mm, "end": v(14.35, -21) * mm});
            skLineSegment(sketch, "E328", {"start": v(14.35, -21) * mm, "end": v(15.43, -20.84) * mm});
            skLineSegment(sketch, "E329", {"start": v(15.43, -20.84) * mm, "end": v(16.47, -20.57) * mm});
            skLineSegment(sketch, "E330", {"start": v(16.47, -20.57) * mm, "end": v(17.45, -20.19) * mm});
            skLineSegment(sketch, "E331", {"start": v(17.45, -20.19) * mm, "end": v(18.34, -19.69) * mm});
            skLineSegment(sketch, "E332", {"start": v(18.34, -19.69) * mm, "end": v(19.14, -19.07) * mm});
            skLineSegment(sketch, "E333", {"start": v(19.14, -19.07) * mm, "end": v(19.82, -18.34) * mm});
            skLineSegment(sketch, "E334", {"start": v(19.82, -18.34) * mm, "end": v(20.37, -17.48) * mm});
            skLineSegment(sketch, "E335", {"start": v(20.37, -17.48) * mm, "end": v(20.76, -16.5) * mm});
            skLineSegment(sketch, "E336", {"start": v(20.76, -16.5) * mm, "end": v(20.77, -16.45) * mm});
            skLineSegment(sketch, "E337", {"start": v(20.77, -16.45) * mm, "end": v(20.8, -16.38) * mm});
            skLineSegment(sketch, "E338", {"start": v(20.8, -16.38) * mm, "end": v(20.82, -16.28) * mm});
            skLineSegment(sketch, "E339", {"start": v(20.82, -16.28) * mm, "end": v(20.86, -16.16) * mm});
            skLineSegment(sketch, "E340", {"start": v(20.86, -16.16) * mm, "end": v(20.9, -16.02) * mm});
            skLineSegment(sketch, "E341", {"start": v(20.9, -16.02) * mm, "end": v(20.93, -15.85) * mm});
            skLineSegment(sketch, "E342", {"start": v(20.93, -15.85) * mm, "end": v(20.96, -15.66) * mm});
            skLineSegment(sketch, "E343", {"start": v(20.96, -15.66) * mm, "end": v(20.99, -15.45) * mm});
            skLineSegment(sketch, "E344", {"start": v(20.99, -15.45) * mm, "end": v(21.01, -15.22) * mm});
            skLineSegment(sketch, "E345", {"start": v(21.01, -15.22) * mm, "end": v(21.03, -14.97) * mm});
            skLineSegment(sketch, "E346", {"start": v(21.03, -14.97) * mm, "end": v(21.04, -14.7) * mm});
            skLineSegment(sketch, "E347", {"start": v(21.04, -14.7) * mm, "end": v(21.04, -14.41) * mm});
            skLineSegment(sketch, "E348", {"start": v(21.04, -14.41) * mm, "end": v(21.03, -14.1) * mm});
            skLineSegment(sketch, "E349", {"start": v(21.03, -14.1) * mm, "end": v(21, -13.78) * mm});
            skLineSegment(sketch, "E350", {"start": v(21, -13.78) * mm, "end": v(20.96, -13.43) * mm});
            skLineSegment(sketch, "E351", {"start": v(20.96, -13.43) * mm, "end": v(20.9, -13.07) * mm});
            skLineSegment(sketch, "E352", {"start": v(2.18, 2.02) * mm, "end": v(1.89, 2.02) * mm});
            skLineSegment(sketch, "E353", {"start": v(1.89, 2.02) * mm, "end": v(1.6, 2.02) * mm});
            skLineSegment(sketch, "E354", {"start": v(1.6, 2.02) * mm, "end": v(1.3, 2.02) * mm});
            skLineSegment(sketch, "E355", {"start": v(1.3, 2.02) * mm, "end": v(1.01, 2.02) * mm});
            skLineSegment(sketch, "E356", {"start": v(1.01, 2.02) * mm, "end": v(0.72, 2.02) * mm});
            skLineSegment(sketch, "E357", {"start": v(0.72, 2.02) * mm, "end": v(0.43, 2.02) * mm});
            skLineSegment(sketch, "E358", {"start": v(0.43, 2.02) * mm, "end": v(0.14, 2.02) * mm});
            skLineSegment(sketch, "E359", {"start": v(0.14, 2.02) * mm, "end": v(-0.16, 2.02) * mm});
            skLineSegment(sketch, "E360", {"start": v(-0.16, 2.02) * mm, "end": v(-0.45, 2.02) * mm});
            skLineSegment(sketch, "E361", {"start": v(-0.45, 2.02) * mm, "end": v(-0.74, 2.02) * mm});
            skLineSegment(sketch, "E362", {"start": v(-0.74, 2.02) * mm, "end": v(-1.03, 2.02) * mm});
            skLineSegment(sketch, "E363", {"start": v(-1.03, 2.02) * mm, "end": v(-1.33, 2.02) * mm});
            skLineSegment(sketch, "E364", {"start": v(-1.33, 2.02) * mm, "end": v(-1.62, 2.02) * mm});
            skLineSegment(sketch, "E365", {"start": v(-1.62, 2.02) * mm, "end": v(-1.91, 2.02) * mm});
            skLineSegment(sketch, "E366", {"start": v(-1.91, 2.02) * mm, "end": v(-2.2, 2.02) * mm});
            skLineSegment(sketch, "E367", {"start": v(-2.2, 2.02) * mm, "end": v(-2.5, 2.02) * mm});
            skLineSegment(sketch, "E368", {"start": v(-2.5, 2.02) * mm, "end": v(-2.5, 1.26) * mm});
            skLineSegment(sketch, "E369", {"start": v(-2.5, 1.26) * mm, "end": v(-2.5, 0.5) * mm});
            skLineSegment(sketch, "E370", {"start": v(-2.5, 0.5) * mm, "end": v(-2.5, -0.25) * mm});
            skLineSegment(sketch, "E371", {"start": v(-2.5, -0.25) * mm, "end": v(-2.5, -1) * mm});
            skLineSegment(sketch, "E372", {"start": v(-2.5, -1) * mm, "end": v(-2.5, -1.76) * mm});
            skLineSegment(sketch, "E373", {"start": v(-2.5, -1.76) * mm, "end": v(-2.5, -2.51) * mm});
            skLineSegment(sketch, "E374", {"start": v(-2.5, -2.51) * mm, "end": v(-2.5, -3.27) * mm});
            skLineSegment(sketch, "E375", {"start": v(-2.5, -3.27) * mm, "end": v(-2.5, -4.03) * mm});
            skLineSegment(sketch, "E376", {"start": v(-2.5, -4.03) * mm, "end": v(-2.5, -4.78) * mm});
            skLineSegment(sketch, "E377", {"start": v(-2.5, -4.78) * mm, "end": v(-2.5, -5.54) * mm});
            skLineSegment(sketch, "E378", {"start": v(-2.5, -5.54) * mm, "end": v(-2.5, -6.3) * mm});
            skLineSegment(sketch, "E379", {"start": v(-2.5, -6.3) * mm, "end": v(-2.5, -7.05) * mm});
            skLineSegment(sketch, "E380", {"start": v(-2.5, -7.05) * mm, "end": v(-2.51, -7.8) * mm});
            skLineSegment(sketch, "E381", {"start": v(-2.51, -7.8) * mm, "end": v(-2.51, -8.56) * mm});
            skLineSegment(sketch, "E382", {"start": v(-2.51, -8.56) * mm, "end": v(-2.51, -9.32) * mm});
            skLineSegment(sketch, "E383", {"start": v(-2.51, -9.32) * mm, "end": v(-2.51, -10.07) * mm});
            skLineSegment(sketch, "E384", {"start": v(-2.51, -10.07) * mm, "end": v(-2.51, -10.55) * mm});
            skLineSegment(sketch, "E385", {"start": v(-2.51, -10.55) * mm, "end": v(-2.5, -11.02) * mm});
            skLineSegment(sketch, "E386", {"start": v(-2.5, -11.02) * mm, "end": v(-2.5, -11.49) * mm});
            skLineSegment(sketch, "E387", {"start": v(-2.5, -11.49) * mm, "end": v(-2.5, -11.94) * mm});
            skLineSegment(sketch, "E388", {"start": v(-2.5, -11.94) * mm, "end": v(-2.5, -12.38) * mm});
            skLineSegment(sketch, "E389", {"start": v(-2.5, -12.38) * mm, "end": v(-2.5, -12.8) * mm});
            skLineSegment(sketch, "E390", {"start": v(-2.5, -12.8) * mm, "end": v(-2.5, -13.2) * mm});
            skLineSegment(sketch, "E391", {"start": v(-2.5, -13.2) * mm, "end": v(-2.5, -13.59) * mm});
            skLineSegment(sketch, "E392", {"start": v(-2.5, -13.59) * mm, "end": v(-2.5, -13.95) * mm});
            skLineSegment(sketch, "E393", {"start": v(-2.5, -13.95) * mm, "end": v(-2.53, -14.3) * mm});
            skLineSegment(sketch, "E394", {"start": v(-2.53, -14.3) * mm, "end": v(-2.55, -14.6) * mm});
            skLineSegment(sketch, "E395", {"start": v(-2.55, -14.6) * mm, "end": v(-2.58, -14.9) * mm});
            skLineSegment(sketch, "E396", {"start": v(-2.58, -14.9) * mm, "end": v(-2.62, -15.15) * mm});
            skLineSegment(sketch, "E397", {"start": v(-2.62, -15.15) * mm, "end": v(-2.67, -15.38) * mm});
            skLineSegment(sketch, "E398", {"start": v(-2.67, -15.38) * mm, "end": v(-2.73, -15.57) * mm});
            skLineSegment(sketch, "E399", {"start": v(-2.73, -15.57) * mm, "end": v(-2.8, -15.72) * mm});
            skLineSegment(sketch, "E400", {"start": v(-2.8, -15.72) * mm, "end": v(-2.94, -15.97) * mm});
            skLineSegment(sketch, "E401", {"start": v(-2.94, -15.97) * mm, "end": v(-3.1, -16.18) * mm});
            skLineSegment(sketch, "E402", {"start": v(-3.1, -16.18) * mm, "end": v(-3.29, -16.36) * mm});
            skLineSegment(sketch, "E403", {"start": v(-3.29, -16.36) * mm, "end": v(-3.48, -16.51) * mm});
            skLineSegment(sketch, "E404", {"start": v(-3.48, -16.51) * mm, "end": v(-3.7, -16.63) * mm});
            skLineSegment(sketch, "E405", {"start": v(-3.7, -16.63) * mm, "end": v(-3.92, -16.73) * mm});
            skLineSegment(sketch, "E406", {"start": v(-3.92, -16.73) * mm, "end": v(-4.15, -16.8) * mm});
            skLineSegment(sketch, "E407", {"start": v(-4.15, -16.8) * mm, "end": v(-4.39, -16.84) * mm});
            skLineSegment(sketch, "E408", {"start": v(-4.39, -16.84) * mm, "end": v(-4.62, -16.87) * mm});
            skLineSegment(sketch, "E409", {"start": v(-4.62, -16.87) * mm, "end": v(-4.86, -16.88) * mm});
            skLineSegment(sketch, "E410", {"start": v(-4.86, -16.88) * mm, "end": v(-5.09, -16.88) * mm});
            skLineSegment(sketch, "E411", {"start": v(-5.09, -16.88) * mm, "end": v(-5.3, -16.86) * mm});
            skLineSegment(sketch, "E412", {"start": v(-5.3, -16.86) * mm, "end": v(-5.52, -16.83) * mm});
            skLineSegment(sketch, "E413", {"start": v(-5.52, -16.83) * mm, "end": v(-5.72, -16.79) * mm});
            skLineSegment(sketch, "E414", {"start": v(-5.72, -16.79) * mm, "end": v(-5.9, -16.74) * mm});
            skLineSegment(sketch, "E415", {"start": v(-5.9, -16.74) * mm, "end": v(-6.06, -16.7) * mm});
            skLineSegment(sketch, "E416", {"start": v(-6.06, -16.7) * mm, "end": v(-6.21, -16.61) * mm});
            skLineSegment(sketch, "E417", {"start": v(-6.21, -16.61) * mm, "end": v(-6.35, -16.53) * mm});
            skLineSegment(sketch, "E418", {"start": v(-6.35, -16.53) * mm, "end": v(-6.49, -16.45) * mm});
            skLineSegment(sketch, "E419", {"start": v(-6.49, -16.45) * mm, "end": v(-6.61, -16.36) * mm});
            skLineSegment(sketch, "E420", {"start": v(-6.61, -16.36) * mm, "end": v(-6.73, -16.26) * mm});
            skLineSegment(sketch, "E421", {"start": v(-6.73, -16.26) * mm, "end": v(-6.84, -16.16) * mm});
            skLineSegment(sketch, "E422", {"start": v(-6.84, -16.16) * mm, "end": v(-6.95, -16.06) * mm});
            skLineSegment(sketch, "E423", {"start": v(-6.95, -16.06) * mm, "end": v(-7.05, -15.95) * mm});
            skLineSegment(sketch, "E424", {"start": v(-7.05, -15.95) * mm, "end": v(-7.15, -15.84) * mm});
            skLineSegment(sketch, "E425", {"start": v(-7.15, -15.84) * mm, "end": v(-7.25, -15.72) * mm});
            skLineSegment(sketch, "E426", {"start": v(-7.25, -15.72) * mm, "end": v(-7.34, -15.6) * mm});
            skLineSegment(sketch, "E427", {"start": v(-7.34, -15.6) * mm, "end": v(-7.43, -15.47) * mm});
            skLineSegment(sketch, "E428", {"start": v(-7.43, -15.47) * mm, "end": v(-7.52, -15.33) * mm});
            skLineSegment(sketch, "E429", {"start": v(-7.52, -15.33) * mm, "end": v(-7.61, -15.2) * mm});
            skLineSegment(sketch, "E430", {"start": v(-7.61, -15.2) * mm, "end": v(-7.7, -15.05) * mm});
            skLineSegment(sketch, "E431", {"start": v(-7.7, -15.05) * mm, "end": v(-7.79, -14.9) * mm});
            skLineSegment(sketch, "E432", {"start": v(-7.79, -14.9) * mm, "end": v(-7.81, -14.86) * mm});
            skLineSegment(sketch, "E433", {"start": v(-7.81, -14.86) * mm, "end": v(-7.84, -14.82) * mm});
            skLineSegment(sketch, "E434", {"start": v(-7.84, -14.82) * mm, "end": v(-7.86, -14.78) * mm});
            skLineSegment(sketch, "E435", {"start": v(-7.86, -14.78) * mm, "end": v(-7.88, -14.74) * mm});
            skLineSegment(sketch, "E436", {"start": v(-7.88, -14.74) * mm, "end": v(-7.9, -14.7) * mm});
            skLineSegment(sketch, "E437", {"start": v(-7.9, -14.7) * mm, "end": v(-7.92, -14.67) * mm});
            skLineSegment(sketch, "E438", {"start": v(-7.92, -14.67) * mm, "end": v(-7.94, -14.63) * mm});
            skLineSegment(sketch, "E439", {"start": v(-7.94, -14.63) * mm, "end": v(-7.96, -14.6) * mm});
            skLineSegment(sketch, "E440", {"start": v(-7.96, -14.6) * mm, "end": v(-7.98, -14.58) * mm});
            skLineSegment(sketch, "E441", {"start": v(-7.98, -14.58) * mm, "end": v(-8, -14.55) * mm});
            skLineSegment(sketch, "E442", {"start": v(-8, -14.55) * mm, "end": v(-8, -14.53) * mm});
            skLineSegment(sketch, "E443", {"start": v(-8, -14.53) * mm, "end": v(-8.02, -14.51) * mm});
            skLineSegment(sketch, "E444", {"start": v(-8.02, -14.51) * mm, "end": v(-8.03, -14.5) * mm});
            skLineSegment(sketch, "E445", {"start": v(-8.03, -14.5) * mm, "end": v(-8.04, -14.49) * mm});
            skLineSegment(sketch, "E446", {"start": v(-8.04, -14.49) * mm, "end": v(-8.05, -14.48) * mm});
            skLineSegment(sketch, "E447", {"start": v(-8.05, -14.48) * mm, "end": v(-8.06, -14.47) * mm});
            skLineSegment(sketch, "E448", {"start": v(-8.06, -14.47) * mm, "end": v(-8.3, -14.62) * mm});
            skLineSegment(sketch, "E449", {"start": v(-8.3, -14.62) * mm, "end": v(-8.53, -14.76) * mm});
            skLineSegment(sketch, "E450", {"start": v(-8.53, -14.76) * mm, "end": v(-8.77, -14.9) * mm});
            skLineSegment(sketch, "E451", {"start": v(-8.77, -14.9) * mm, "end": v(-9, -15.05) * mm});
            skLineSegment(sketch, "E452", {"start": v(-9, -15.05) * mm, "end": v(-9.24, -15.2) * mm});
            skLineSegment(sketch, "E453", {"start": v(-9.24, -15.2) * mm, "end": v(-9.48, -15.35) * mm});
            skLineSegment(sketch, "E454", {"start": v(-9.48, -15.35) * mm, "end": v(-9.72, -15.5) * mm});
            skLineSegment(sketch, "E455", {"start": v(-9.72, -15.5) * mm, "end": v(-9.96, -15.64) * mm});
            skLineSegment(sketch, "E456", {"start": v(-9.96, -15.64) * mm, "end": v(-10.2, -15.78) * mm});
            skLineSegment(sketch, "E457", {"start": v(-10.2, -15.78) * mm, "end": v(-10.43, -15.93) * mm});
            skLineSegment(sketch, "E458", {"start": v(-10.43, -15.93) * mm, "end": v(-10.67, -16.07) * mm});
            skLineSegment(sketch, "E459", {"start": v(-10.67, -16.07) * mm, "end": v(-10.9, -16.22) * mm});
            skLineSegment(sketch, "E460", {"start": v(-10.9, -16.22) * mm, "end": v(-11.15, -16.36) * mm});
            skLineSegment(sketch, "E461", {"start": v(-11.15, -16.36) * mm, "end": v(-11.38, -16.5) * mm});
            skLineSegment(sketch, "E462", {"start": v(-11.38, -16.5) * mm, "end": v(-11.62, -16.66) * mm});
            skLineSegment(sketch, "E463", {"start": v(-11.62, -16.66) * mm, "end": v(-11.86, -16.8) * mm});
            skLineSegment(sketch, "E464", {"start": v(-11.86, -16.8) * mm, "end": v(-11.74, -17.04) * mm});
            skLineSegment(sketch, "E465", {"start": v(-11.74, -17.04) * mm, "end": v(-11.6, -17.28) * mm});
            skLineSegment(sketch, "E466", {"start": v(-11.6, -17.28) * mm, "end": v(-11.47, -17.51) * mm});
            skLineSegment(sketch, "E467", {"start": v(-11.47, -17.51) * mm, "end": v(-11.33, -17.74) * mm});
            skLineSegment(sketch, "E468", {"start": v(-11.33, -17.74) * mm, "end": v(-11.18, -17.96) * mm});
            skLineSegment(sketch, "E469", {"start": v(-11.18, -17.96) * mm, "end": v(-11.02, -18.18) * mm});
            skLineSegment(sketch, "E470", {"start": v(-11.02, -18.18) * mm, "end": v(-10.86, -18.39) * mm});
            skLineSegment(sketch, "E471", {"start": v(-10.86, -18.39) * mm, "end": v(-10.7, -18.6) * mm});
            skLineSegment(sketch, "E472", {"start": v(-10.7, -18.6) * mm, "end": v(-10.51, -18.79) * mm});
            skLineSegment(sketch, "E473", {"start": v(-10.51, -18.79) * mm, "end": v(-10.33, -18.98) * mm});
            skLineSegment(sketch, "E474", {"start": v(-10.33, -18.98) * mm, "end": v(-10.14, -19.16) * mm});
            skLineSegment(sketch, "E475", {"start": v(-10.14, -19.16) * mm, "end": v(-9.95, -19.34) * mm});
            skLineSegment(sketch, "E476", {"start": v(-9.95, -19.34) * mm, "end": v(-9.74, -19.5) * mm});
            skLineSegment(sketch, "E477", {"start": v(-9.74, -19.5) * mm, "end": v(-9.54, -19.66) * mm});
            skLineSegment(sketch, "E478", {"start": v(-9.54, -19.66) * mm, "end": v(-9.32, -19.81) * mm});
            skLineSegment(sketch, "E479", {"start": v(-9.32, -19.81) * mm, "end": v(-9.1, -19.96) * mm});
            skLineSegment(sketch, "E480", {"start": v(-9.1, -19.96) * mm, "end": v(-8.76, -20.15) * mm});
            skLineSegment(sketch, "E481", {"start": v(-8.76, -20.15) * mm, "end": v(-8.4, -20.32) * mm});
            skLineSegment(sketch, "E482", {"start": v(-8.4, -20.32) * mm, "end": v(-8.04, -20.48) * mm});
            skLineSegment(sketch, "E483", {"start": v(-8.04, -20.48) * mm, "end": v(-7.66, -20.62) * mm});
            skLineSegment(sketch, "E484", {"start": v(-7.66, -20.62) * mm, "end": v(-7.27, -20.74) * mm});
            skLineSegment(sketch, "E485", {"start": v(-7.27, -20.74) * mm, "end": v(-6.86, -20.84) * mm});
            skLineSegment(sketch, "E486", {"start": v(-6.86, -20.84) * mm, "end": v(-6.45, -20.92) * mm});
            skLineSegment(sketch, "E487", {"start": v(-6.45, -20.92) * mm, "end": v(-6.03, -20.98) * mm});
            skLineSegment(sketch, "E488", {"start": v(-6.03, -20.98) * mm, "end": v(-5.6, -21.03) * mm});
            skLineSegment(sketch, "E489", {"start": v(-5.6, -21.03) * mm, "end": v(-5.16, -21.05) * mm});
            skLineSegment(sketch, "E490", {"start": v(-5.16, -21.05) * mm, "end": v(-4.72, -21.06) * mm});
            skLineSegment(sketch, "E491", {"start": v(-4.72, -21.06) * mm, "end": v(-4.27, -21.04) * mm});
            skLineSegment(sketch, "E492", {"start": v(-4.27, -21.04) * mm, "end": v(-3.81, -21) * mm});
            skLineSegment(sketch, "E493", {"start": v(-3.81, -21) * mm, "end": v(-3.35, -20.95) * mm});
            skLineSegment(sketch, "E494", {"start": v(-3.35, -20.95) * mm, "end": v(-2.89, -20.88) * mm});
            skLineSegment(sketch, "E495", {"start": v(-2.89, -20.88) * mm, "end": v(-2.42, -20.78) * mm});
            skLineSegment(sketch, "E496", {"start": v(-2.42, -20.78) * mm, "end": v(-2.12, -20.68) * mm});
            skLineSegment(sketch, "E497", {"start": v(-2.12, -20.68) * mm, "end": v(-1.82, -20.58) * mm});
            skLineSegment(sketch, "E498", {"start": v(-1.82, -20.58) * mm, "end": v(-1.53, -20.46) * mm});
            skLineSegment(sketch, "E499", {"start": v(-1.53, -20.46) * mm, "end": v(-1.25, -20.33) * mm});
            skLineSegment(sketch, "E500", {"start": v(-1.25, -20.33) * mm, "end": v(-0.97, -20.18) * mm});
            skLineSegment(sketch, "E501", {"start": v(-0.97, -20.18) * mm, "end": v(-0.7, -20.03) * mm});
            skLineSegment(sketch, "E502", {"start": v(-0.7, -20.03) * mm, "end": v(-0.45, -19.86) * mm});
            skLineSegment(sketch, "E503", {"start": v(-0.45, -19.86) * mm, "end": v(-0.2, -19.68) * mm});
            skLineSegment(sketch, "E504", {"start": v(-0.2, -19.68) * mm, "end": v(0.04, -19.5) * mm});
            skLineSegment(sketch, "E505", {"start": v(0.04, -19.5) * mm, "end": v(0.27, -19.3) * mm});
            skLineSegment(sketch, "E506", {"start": v(0.27, -19.3) * mm, "end": v(0.48, -19.08) * mm});
            skLineSegment(sketch, "E507", {"start": v(0.48, -19.08) * mm, "end": v(0.68, -18.85) * mm});
            skLineSegment(sketch, "E508", {"start": v(0.68, -18.85) * mm, "end": v(0.87, -18.61) * mm});
            skLineSegment(sketch, "E509", {"start": v(0.87, -18.61) * mm, "end": v(1.05, -18.36) * mm});
            skLineSegment(sketch, "E510", {"start": v(1.05, -18.36) * mm, "end": v(1.2, -18.1) * mm});
            skLineSegment(sketch, "E511", {"start": v(1.2, -18.1) * mm, "end": v(1.35, -17.82) * mm});
            skLineSegment(sketch, "E512", {"start": v(1.35, -17.82) * mm, "end": v(1.54, -17.45) * mm});
            skLineSegment(sketch, "E513", {"start": v(1.54, -17.45) * mm, "end": v(1.7, -17.07) * mm});
            skLineSegment(sketch, "E514", {"start": v(1.7, -17.07) * mm, "end": v(1.83, -16.68) * mm});
            skLineSegment(sketch, "E515", {"start": v(1.83, -16.68) * mm, "end": v(1.93, -16.28) * mm});
            skLineSegment(sketch, "E516", {"start": v(1.93, -16.28) * mm, "end": v(2.02, -15.87) * mm});
            skLineSegment(sketch, "E517", {"start": v(2.02, -15.87) * mm, "end": v(2.09, -15.45) * mm});
            skLineSegment(sketch, "E518", {"start": v(2.09, -15.45) * mm, "end": v(2.14, -15.02) * mm});
            skLineSegment(sketch, "E519", {"start": v(2.14, -15.02) * mm, "end": v(2.17, -14.59) * mm});
            skLineSegment(sketch, "E520", {"start": v(2.17, -14.59) * mm, "end": v(2.2, -14.15) * mm});
            skLineSegment(sketch, "E521", {"start": v(2.2, -14.15) * mm, "end": v(2.2, -13.7) * mm});
            skLineSegment(sketch, "E522", {"start": v(2.2, -13.7) * mm, "end": v(2.2, -13.24) * mm});
            skLineSegment(sketch, "E523", {"start": v(2.2, -13.24) * mm, "end": v(2.2, -12.78) * mm});
            skLineSegment(sketch, "E524", {"start": v(2.2, -12.78) * mm, "end": v(2.2, -12.3) * mm});
            skLineSegment(sketch, "E525", {"start": v(2.2, -12.3) * mm, "end": v(2.2, -11.83) * mm});
            skLineSegment(sketch, "E526", {"start": v(2.2, -11.83) * mm, "end": v(2.19, -11.35) * mm});
            skLineSegment(sketch, "E527", {"start": v(2.19, -11.35) * mm, "end": v(2.18, -10.86) * mm});
            skLineSegment(sketch, "E528", {"start": v(2.18, -10.86) * mm, "end": v(2.19, -10.05) * mm});
            skLineSegment(sketch, "E529", {"start": v(2.19, -10.05) * mm, "end": v(2.19, -9.25) * mm});
            skLineSegment(sketch, "E530", {"start": v(2.19, -9.25) * mm, "end": v(2.2, -8.44) * mm});
            skLineSegment(sketch, "E531", {"start": v(2.2, -8.44) * mm, "end": v(2.2, -7.64) * mm});
            skLineSegment(sketch, "E532", {"start": v(2.2, -7.64) * mm, "end": v(2.2, -6.84) * mm});
            skLineSegment(sketch, "E533", {"start": v(2.2, -6.84) * mm, "end": v(2.2, -6.03) * mm});
            skLineSegment(sketch, "E534", {"start": v(2.2, -6.03) * mm, "end": v(2.2, -5.23) * mm});
            skLineSegment(sketch, "E535", {"start": v(2.2, -5.23) * mm, "end": v(2.2, -4.42) * mm});
            skLineSegment(sketch, "E536", {"start": v(2.2, -4.42) * mm, "end": v(2.19, -3.62) * mm});
            skLineSegment(sketch, "E537", {"start": v(2.19, -3.62) * mm, "end": v(2.19, -2.81) * mm});
            skLineSegment(sketch, "E538", {"start": v(2.19, -2.81) * mm, "end": v(2.19, -2) * mm});
            skLineSegment(sketch, "E539", {"start": v(2.19, -2) * mm, "end": v(2.18, -1.2) * mm});
            skLineSegment(sketch, "E540", {"start": v(2.18, -1.2) * mm, "end": v(2.18, -0.4) * mm});
            skLineSegment(sketch, "E541", {"start": v(2.18, -0.4) * mm, "end": v(2.18, 0.4) * mm});
            skLineSegment(sketch, "E542", {"start": v(2.18, 0.4) * mm, "end": v(2.18, 1.21) * mm});
            skLineSegment(sketch, "E543", {"start": v(2.18, 1.21) * mm, "end": v(2.18, 2.02) * mm});
            skSolve(sketch);
        }
        {
            var Q0;
            Q0=makeQuery(id+"F0.imprint","IMPRINT",FACE,{"disambiguationData":[TD([[makeQuery(id+"F0.imprint","IMPRINT",EDGE,{"derivedFrom":sQuery(id+"F0.wireOp",EDGE,"E0")}),-1.0]])]});
            extrude(context, id + "F1", {"entities" : qUnion([Q0]), "depth" : 5 * mm});
        }
        {
            var Q0;
            Q0=makeQuery(id+"F1.opExtrude","SWEPT_FACE",FACE,{"disambiguationData":[OSD([sQuery(id+"F0.wireOp",EDGE,"E16"),sQuery(id+"F0.wireOp",EDGE,"E17"),sQuery(id+"F0.wireOp",EDGE,"E18"),sQuery(id+"F0.wireOp",EDGE,"E19"),sQuery(id+"F0.wireOp",EDGE,"E20"),sQuery(id+"F0.wireOp",EDGE,"E21"),sQuery(id+"F0.wireOp",EDGE,"E22"),sQuery(id+"F0.wireOp",EDGE,"E23"),sQuery(id+"F0.wireOp",EDGE,"E24"),sQuery(id+"F0.wireOp",EDGE,"E25"),sQuery(id+"F0.wireOp",EDGE,"E26"),sQuery(id+"F0.wireOp",EDGE,"E27"),sQuery(id+"F0.wireOp",EDGE,"E28"),sQuery(id+"F0.wireOp",EDGE,"E29"),sQuery(id+"F0.wireOp",EDGE,"E30"),sQuery(id+"F0.wireOp",EDGE,"E31")])]});
            var sketch = newSketch(context, id + "F2", { "sketchPlane" : qUnion([Q0])});
            skLineSegment(sketch, "E544", {"start": v(0, -25) * mm, "end": v(-5, -25) * mm});
            skLineSegment(sketch, "E545", {"start": v(-5, -25) * mm, "end": v(-7.5, -32.5) * mm});
            skLineSegment(sketch, "E546", {"start": v(-7.5, -32.5) * mm, "end": v(-10, -32.5) * mm});
            skLineSegment(sketch, "E547", {"start": v(-10, -32.5) * mm, "end": v(-10, -35) * mm});
            skLineSegment(sketch, "E548", {"start": v(-10, -35) * mm, "end": v(5, -35) * mm});
            skLineSegment(sketch, "E549", {"start": v(5, -35) * mm, "end": v(5, -32.5) * mm});
            skLineSegment(sketch, "E550", {"start": v(5, -32.5) * mm, "end": v(2.5, -32.5) * mm});
            skLineSegment(sketch, "E551", {"start": v(2.5, -32.5) * mm, "end": v(0, -25) * mm});
            skLineSegment(sketch, "E552", {"start": v(-2.5, -25) * mm, "end": v(-2.5, -35) * mm});
            skSolve(sketch);
        }
        {
            var Q0;
            {var subQ0=sQuery(id+"F2.wireOp",EDGE,"E549");Q0=makeQuery(id+"F2.imprint","IMPRINT",FACE,{"disambiguationData":[TD([[makeQuery(id+"F2.imprint","IMPRINT",EDGE,{"derivedFrom":subQ0}),1.0]])]});}
            var Q1;
            {var subQ2=sQuery(id+"F2.wireOp",EDGE,"E545");Q1=makeQuery(id+"F2.imprint","IMPRINT",FACE,{"disambiguationData":[TD([[makeQuery(id+"F2.imprint","IMPRINT",EDGE,{"derivedFrom":subQ2}),1.0]])]});}
            var Q2;
            Q2=makeQuery(id+"F1.opExtrude","SWEPT_FACE",FACE,{"disambiguationData":[OSD([sQuery(id+"F0.wireOp",EDGE,"E48"),sQuery(id+"F0.wireOp",EDGE,"E49")])]});
            extrude(context, id + "F3", {"entities" : qUnion([Q0, Q1]), "operationType" : NewBodyOperationType.ADD, "endBound" : BoundingType.UP_TO_SURFACE, "oppositeDirection" : true, "endBoundEntityFace" : qUnion([Q2]), "depth" : 25 * mm});
        }
    });
